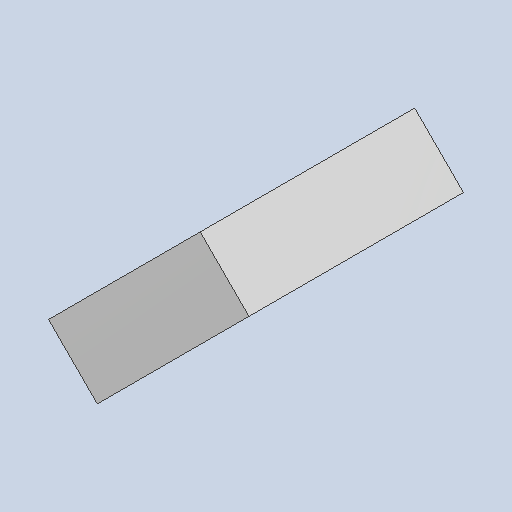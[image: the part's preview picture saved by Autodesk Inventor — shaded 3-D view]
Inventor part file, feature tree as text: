
AUTODESK INVENTOR PART (.ipt)
format: ipt  version: 2023.4 (Build 274418000, 418)  size: 79,360 bytes
history: native  units: mm
features: extrude x1
ambient origin geometry x8: Origin, YZ Plane, XZ Plane, XY Plane, X Axis, Y Axis, Z Axis, Center Point
bodies: Solid1 (feature_tree)
feature tree (1):
  extrude  "Extruded"  [1 undecoded]
note: 1 required parameter value undecoded (feature->parameter linkage not recoverable at this tier; creation-order binding heuristic only, values carry confidence <= 0.55)
